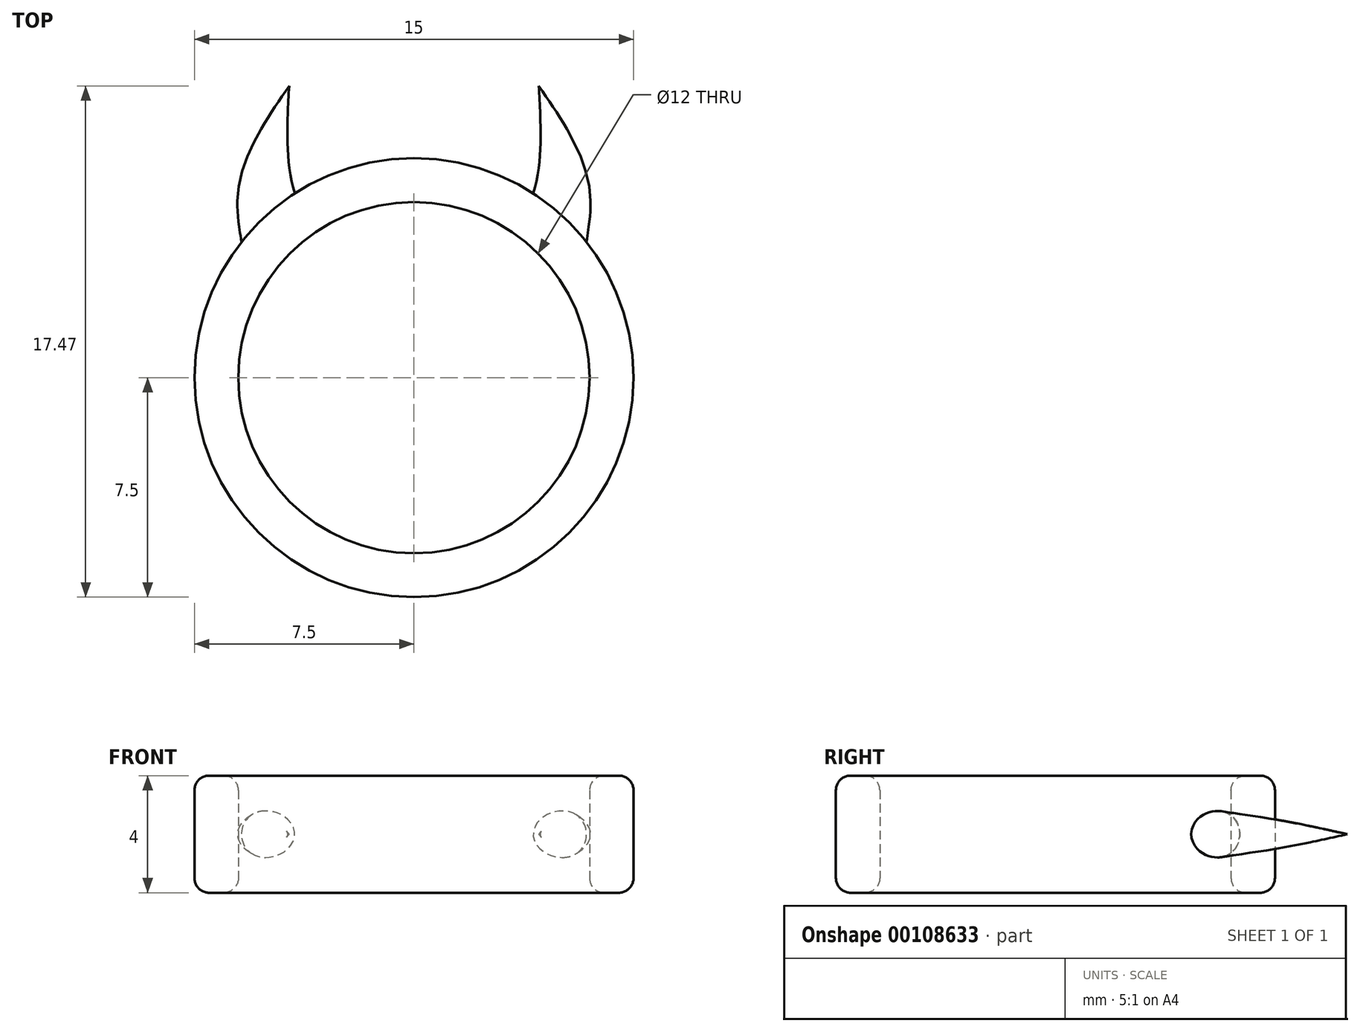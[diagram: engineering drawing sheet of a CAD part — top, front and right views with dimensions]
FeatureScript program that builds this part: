
annotation { "Feature Type Name" : "Feature", "Feature Type Description" : "" }
export const myFeature = defineFeature(function(context is Context, id is Id, definition is map)
    precondition{}
    {
        {
            var Q0;
            Q0=qCreatedBy(makeId("Top.planeOp"),FACE);
            var sketch = newSketch(context, id + "F0", { "sketchPlane" : qUnion([Q0])});
            skCircle(sketch, "E0", {"center": v(0, 0) * mm, "radius": 6 * mm});
            skCircle(sketch, "E1", {"center": v(0, 0) * mm, "radius": 7.5 * mm});
            skPoint(sketch, "E2", {"position": v(-4.26, 9.97) * mm});
            skPoint(sketch, "E3.MirrorP", {"position": v(4.26, 9.97) * mm});
            skSolve(sketch);
        }
        {
            var Q0;
            Q0 = qSketchRegion(id + "F0", true);
            extrude(context, id + "F1", {"entities" : qUnion([Q0]), "endBound" : BoundingType.SYMMETRIC, "depth" : 4 * mm});
        }
        {
            var Q0;
            Q0=makeQuery(id+"F1.opExtrude","CAP_EDGE",EDGE,{"disambiguationData":[OSD([sQuery(id+"F0.wireOp",EDGE,"E0")])],"isStart":true});
            var Q1;
            Q1=makeQuery(id+"F1.opExtrude","CAP_EDGE",EDGE,{"disambiguationData":[OSD([sQuery(id+"F0.wireOp",EDGE,"E0")])],"isStart":false});
            var Q2;
            Q2=makeQuery(id+"F1.opExtrude","CAP_EDGE",EDGE,{"disambiguationData":[OSD([sQuery(id+"F0.wireOp",EDGE,"E1")])],"isStart":false});
            var Q3;
            Q3=makeQuery(id+"F1.opExtrude","CAP_EDGE",EDGE,{"disambiguationData":[OSD([sQuery(id+"F0.wireOp",EDGE,"E1")])],"isStart":true});
            fillet(context, id + "F2", {"entities" : qUnion([Q0, Q1, Q2, Q3]), "radius" : 0.5 * mm, "tangentPropagation" : true, "allowEdgeOverflow" : false});
        }
        {
            var Q0;
            Q0=qCreatedBy(makeId("Front.planeOp"),FACE);
            cPlane(context, id + "F3", {"entities" : qUnion([Q0]), "cplaneType" : CPlaneType.OFFSET, "offset" : 3 * mm, "oppositeDirection" : true, "width" : 150 * mm, "height" : 150 * mm});
        }
        {
            var Q0;
            Q0=qCreatedBy(id+"F3.planeOp",FACE);
            var sketch = newSketch(context, id + "F4", { "sketchPlane" : qUnion([Q0])});
            skEllipse(sketch, "E4", {"center": v(-3.5, 0) * mm, "majorRadius": 2.14 * mm, "minorRadius": 1.51 * mm, "majorAxis": v(-1, 0)});
            skEllipse(sketch, "E5.MirrorC", {"center": v(3.5, 0) * mm, "majorRadius": 2.14 * mm, "minorRadius": 1.51 * mm, "majorAxis": v(1, 0)});
            skSolve(sketch);
        }
        {
            var Q0;
            Q0=qCreatedBy(makeId("Front.planeOp"),FACE);
            cPlane(context, id + "F5", {"entities" : qUnion([Q0]), "cplaneType" : CPlaneType.OFFSET, "offset" : 6 * mm, "oppositeDirection" : true, "width" : 150 * mm, "height" : 150 * mm});
        }
        {
            var Q0;
            Q0=qCreatedBy(id+"F5.planeOp",FACE);
            var sketch = newSketch(context, id + "F6", { "sketchPlane" : qUnion([Q0])});
            skEllipse(sketch, "E6", {"center": v(-5, 0) * mm, "majorRadius": 1.03 * mm, "minorRadius": 0.73 * mm, "majorAxis": v(-1, 0)});
            skEllipse(sketch, "E7.MirrorC", {"center": v(5, 0) * mm, "majorRadius": 1.03 * mm, "minorRadius": 0.73 * mm, "majorAxis": v(1, 0)});
            skSolve(sketch);
        }
        {
            var Q1;
            Q1=makeQuery(id+"F4.imprint","IMPRINT",FACE,{"disambiguationData":[TD([[makeQuery(id+"F4.imprint","IMPRINT",EDGE,{"derivedFrom":sQuery(id+"F4.wireOp",EDGE,"E4")}),1.0]])]});
            var Q2;
            Q2=makeQuery(id+"F6.imprint","IMPRINT",FACE,{"disambiguationData":[TD([[makeQuery(id+"F6.imprint","IMPRINT",EDGE,{"derivedFrom":sQuery(id+"F6.wireOp",EDGE,"E6")}),1.0]])]});
            var Q3;
            Q3=sQuery(id+"F0.wireOp",VERTEX,"E2");
            loft(context, id + "F7", {"operationType" : NewBodyOperationType.ADD, "sheetProfilesArray" : [{ "sheetProfileEntities" : qUnion([Q1]) }, { "sheetProfileEntities" : qUnion([Q2]) }, { "sheetProfileEntities" : qUnion([Q3]) }]});
        }
        {
            var Q1;
            Q1=makeQuery(id+"F4.imprint","IMPRINT",FACE,{"disambiguationData":[TD([[makeQuery(id+"F4.imprint","IMPRINT",EDGE,{"derivedFrom":sQuery(id+"F4.wireOp",EDGE,"E5.MirrorC")}),1.0]])]});
            var Q2;
            Q2=makeQuery(id+"F6.imprint","IMPRINT",FACE,{"disambiguationData":[TD([[makeQuery(id+"F6.imprint","IMPRINT",EDGE,{"derivedFrom":sQuery(id+"F6.wireOp",EDGE,"E7.MirrorC")}),1.0]])]});
            var Q3;
            Q3=sQuery(id+"F0.wireOp",VERTEX,"E3.MirrorP");
            loft(context, id + "F8", {"operationType" : NewBodyOperationType.ADD, "sheetProfilesArray" : [{ "sheetProfileEntities" : qUnion([Q1]) }, { "sheetProfileEntities" : qUnion([Q2]) }, { "sheetProfileEntities" : qUnion([Q3]) }]});
        }
        {
            var Q0;
            Q0=makeQuery(id+"F0.imprint","IMPRINT",FACE,{"disambiguationData":[TD([[makeQuery(id+"F0.imprint","IMPRINT",EDGE,{"derivedFrom":sQuery(id+"F0.wireOp",EDGE,"E0")}),1.0]])]});
            extrude(context, id + "F9", {"entities" : qUnion([Q0]), "operationType" : NewBodyOperationType.REMOVE, "endBound" : BoundingType.SYMMETRIC, "oppositeDirection" : true, "depth" : 5 * mm});
        }
    });
